# Revit family: Champagne Bubbles LED Pendant
name_source: partatom
category: Luminárias
units: mm (PartAtom-declared; Revit-internal decimal feet)

## family parameters
Com base no plano de trabalho = Sim
Compartilhado = Não
Corte com vazios quando carregada = Não
Cota do conector redondo = Utilizar diâmetro
Fonte luminosa = Sim
Número OmniClass = 23.80.70.00
Ponto de cálculo do ambiente = Não
Sempre na vertical = Não
Tipo de parte = Normal
Título OmniClass = Lighting

## types (1)
- Champagne Bubbles LED Pendant
    Arquivo de rede fotométrica = 2961.ies
    Elevação-padrão = 1219
    Fabricante = SONNEMAN
    Filtro de cor = 16777215
    Glass = Seeded Glass
    Modelo = Champagne Bubble LED Pendant
    Specs = https://sonnemanlight.com
    Structure = Polished Chrome
    Troca de temperatura da cor de lâmpada com esmaecimento = <Nenhum>
    URL = https://sonnemanlight.com
    White glass = White glass
    Ângulo de inclinação = 90.00°

## geometry (parser evidence)
native form markers: Blend x6
no freeform markers — native parametric forms only
